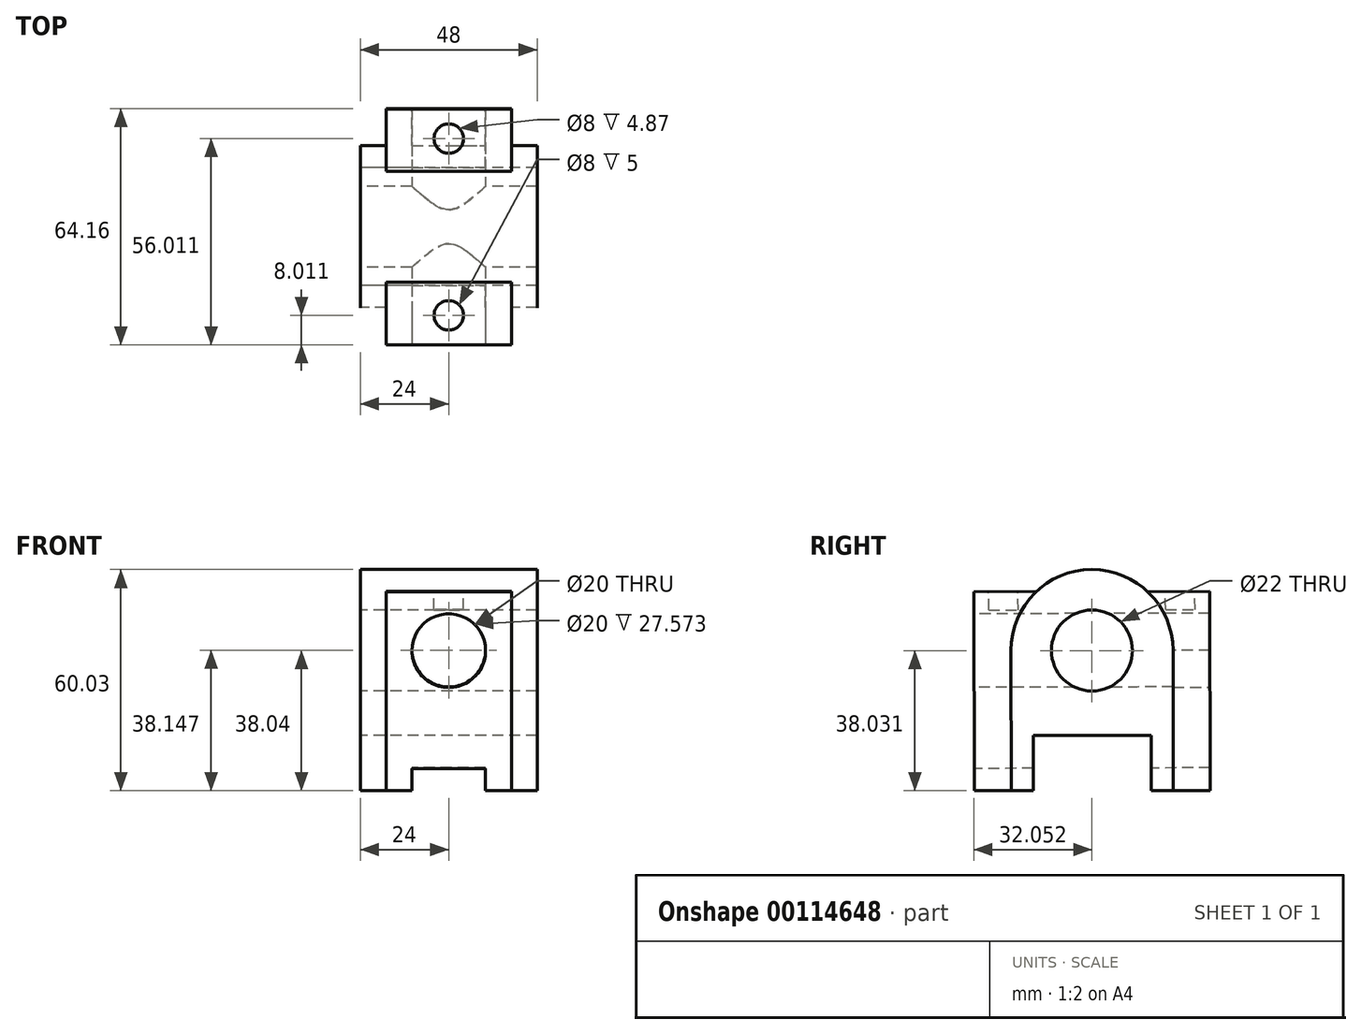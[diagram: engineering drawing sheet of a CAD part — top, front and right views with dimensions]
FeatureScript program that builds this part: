
annotation { "Feature Type Name" : "Feature", "Feature Type Description" : "" }
export const myFeature = defineFeature(function(context is Context, id is Id, definition is map)
    precondition{}
    {
        {
            var Q0;
            Q0=qCreatedBy(makeId("Right.planeOp"),FACE);
            var sketch = newSketch(context, id + "F0", { "sketchPlane" : qUnion([Q0])});
            skLineSegment(sketch, "E0.bottom", {"start": v(29.56, -52.26) * mm, "end": v(23.52, -52.26) * mm});
            skLineSegment(sketch, "E0.left", {"start": v(29.56, -52.26) * mm, "end": v(29.45, -14.14) * mm});
            skLineSegment(sketch, "E0.right", {"start": v(-14.44, -52.26) * mm, "end": v(-14.55, -14.25) * mm});
            skArc(sketch, "E1", {"start": v(29.45, -14.14) * mm, "mid": v(7.4, 7.74) * mm, "end": v(-14.55, -14.25) * mm});
            skLineSegment(sketch, "E2.top", {"start": v(23.52, -37.26) * mm, "end": v(-8.48, -37.26) * mm});
            skLineSegment(sketch, "E2.left", {"start": v(23.52, -52.26) * mm, "end": v(23.52, -37.26) * mm});
            skLineSegment(sketch, "E2.right", {"start": v(-8.48, -52.26) * mm, "end": v(-8.48, -37.26) * mm});
            skPoint(sketch, "E3", {"position": v(7.56, -52.26) * mm});
            skPoint(sketch, "E4", {"position": v(7.52, -37.26) * mm});
            skLineSegment(sketch, "E5.trimOffspring", {"start": v(-8.48, -52.26) * mm, "end": v(-14.44, -52.26) * mm});
            skCircle(sketch, "E6", {"center": v(7.45, -14.26) * mm, "radius": 11 * mm});
            skSolve(sketch);
        }
        {
            var Q0;
            Q0 = qSketchRegion(id + "F0", true);
            extrude(context, id + "F1", {"entities" : qUnion([Q0]), "endBound" : BoundingType.SYMMETRIC, "depth" : 48 * mm});
        }
        {
            var Q0;
            Q0=makeQuery(id+"F1.opExtrude","SWEPT_FACE",FACE,{"disambiguationData":[OSD([sQuery(id+"F0.wireOp",EDGE,"E0.right")])]});
            cPlane(context, id + "F2", {"entities" : qUnion([Q0]), "cplaneType" : CPlaneType.OFFSET, "offset" : 10 * mm, "width" : 150 * mm, "height" : 150 * mm});
        }
        {
            var Q0;
            Q0=qCreatedBy(id+"F2.planeOp",FACE);
            var sketch = newSketch(context, id + "F3", { "sketchPlane" : qUnion([Q0])});
            skLineSegment(sketch, "E7.top", {"start": v(-10, -46.22) * mm, "end": v(10, -46.22) * mm});
            skLineSegment(sketch, "E7.left", {"start": v(-10, -52.22) * mm, "end": v(-10, -46.22) * mm});
            skLineSegment(sketch, "E7.right", {"start": v(10, -52.22) * mm, "end": v(10, -46.22) * mm});
            skLineSegment(sketch, "E8", {"start": v(-17, -52.22) * mm, "end": v(-17, 1.78) * mm});
            skLineSegment(sketch, "E9", {"start": v(-17, 1.78) * mm, "end": v(17, 1.78) * mm});
            skLineSegment(sketch, "E10", {"start": v(17, 1.78) * mm, "end": v(17, -52.22) * mm});
            skLineSegment(sketch, "E11", {"start": v(17, -52.22) * mm, "end": v(10, -52.22) * mm});
            skPoint(sketch, "E12", {"position": v(0, -52.22) * mm});
            skCircle(sketch, "E13", {"center": v(0, -14.22) * mm, "radius": 10 * mm});
            skLineSegment(sketch, "E14.trimOffspring", {"start": v(-10, -52.22) * mm, "end": v(-17, -52.22) * mm});
            skSolve(sketch);
        }
        {
            var Q0;
            Q0=makeQuery(id+"F3.imprint","IMPRINT",FACE,{"disambiguationData":[TD([[makeQuery(id+"F3.imprint","IMPRINT",EDGE,{"derivedFrom":sQuery(id+"F3.wireOp",EDGE,"E7.top")}),1.0]])]});
            extrude(context, id + "F4", {"entities" : qUnion([Q0]), "operationType" : NewBodyOperationType.ADD, "endBound" : BoundingType.UP_TO_NEXT, "oppositeDirection" : true, "depth" : 25 * mm});
        }
        {
            var Q0;
            Q0=makeQuery(id+"F1.opExtrude","SWEPT_FACE",FACE,{"disambiguationData":[OSD([sQuery(id+"F0.wireOp",EDGE,"E0.left")])]});
            cPlane(context, id + "F5", {"entities" : qUnion([Q0]), "cplaneType" : CPlaneType.OFFSET, "offset" : 10 * mm, "width" : 150 * mm, "height" : 150 * mm});
        }
        {
            var Q0;
            Q0=qCreatedBy(id+"F5.planeOp",FACE);
            var sketch = newSketch(context, id + "F6", { "sketchPlane" : qUnion([Q0])});
            skLineSegment(sketch, "E15.bottom", {"start": v(-17, -52.35) * mm, "end": v(-10, -52.35) * mm});
            skLineSegment(sketch, "E15.top", {"start": v(-17, 1.65) * mm, "end": v(17, 1.65) * mm});
            skLineSegment(sketch, "E15.left", {"start": v(-17, -52.35) * mm, "end": v(-17, 1.65) * mm});
            skLineSegment(sketch, "E15.right", {"start": v(17, -52.35) * mm, "end": v(17, 1.65) * mm});
            skLineSegment(sketch, "E16.top", {"start": v(-10, -46.35) * mm, "end": v(10, -46.35) * mm});
            skLineSegment(sketch, "E16.left", {"start": v(-10, -52.35) * mm, "end": v(-10, -46.35) * mm});
            skLineSegment(sketch, "E16.right", {"start": v(10, -52.35) * mm, "end": v(10, -46.35) * mm});
            skPoint(sketch, "E17", {"position": v(0, -46.35) * mm});
            skCircle(sketch, "E18", {"center": v(0, -14.35) * mm, "radius": 10 * mm});
            skLineSegment(sketch, "E19.trimOffspring", {"start": v(10, -52.35) * mm, "end": v(17, -52.35) * mm});
            skSolve(sketch);
        }
        {
            var Q0;
            Q0 = qSketchRegion(id + "F6", true);
            extrude(context, id + "F7", {"entities" : qUnion([Q0]), "operationType" : NewBodyOperationType.ADD, "endBound" : BoundingType.UP_TO_NEXT, "oppositeDirection" : true, "depth" : 25 * mm});
        }
        {
            var Q0;
            Q0=makeQuery(id+"F4.opExtrude","SWEPT_FACE",FACE,{"disambiguationData":[OSD([sQuery(id+"F3.wireOp",EDGE,"E9")])]});
            var sketch = newSketch(context, id + "F8", { "sketchPlane" : qUnion([Q0])});
            skCircle(sketch, "E20", {"center": v(0, -16.6) * mm, "radius": 4 * mm});
            skCircle(sketch, "E21", {"center": v(0, 31.4) * mm, "radius": 4 * mm});
            skSolve(sketch);
        }
        {
            var Q0;
            Q0 = qSketchRegion(id + "F8", true);
            extrude(context, id + "F9", {"entities" : qUnion([Q0]), "operationType" : NewBodyOperationType.REMOVE, "oppositeDirection" : true, "depth" : 5 * mm});
        }
        {
            var Q0;
            Q0=makeQuery(id+"F4.opExtrude","CAP_FACE",FACE,{"disambiguationData":[OSD([sQuery(id+"F3.wireOp",EDGE,"E7.top"),sQuery(id+"F3.wireOp",EDGE,"E7.left"),sQuery(id+"F3.wireOp",EDGE,"E7.right"),sQuery(id+"F3.wireOp",EDGE,"E8"),sQuery(id+"F3.wireOp",EDGE,"E9"),sQuery(id+"F3.wireOp",EDGE,"E10"),sQuery(id+"F3.wireOp",EDGE,"E11"),sQuery(id+"F3.wireOp",EDGE,"E13"),sQuery(id+"F3.wireOp",EDGE,"E14.trimOffspring")])],"isStart":true});
            var sketch = newSketch(context, id + "F10", { "sketchPlane" : qUnion([Q0])});
            skCircle(sketch, "E22", {"center": v(0, -14.22) * mm, "radius": 10 * mm});
            skLineSegment(sketch, "E23.top", {"start": v(-10, -46.22) * mm, "end": v(10, -46.22) * mm});
            skLineSegment(sketch, "E23.left", {"start": v(-10, -52.22) * mm, "end": v(-10, -46.22) * mm});
            skLineSegment(sketch, "E23.right", {"start": v(10, -52.22) * mm, "end": v(10, -46.22) * mm});
            skLineSegment(sketch, "E24.top", {"start": v(10, -63.31) * mm, "end": v(-10, -63.31) * mm});
            skLineSegment(sketch, "E24.left", {"start": v(10, -52.22) * mm, "end": v(10, -63.31) * mm});
            skLineSegment(sketch, "E24.right", {"start": v(-10, -52.22) * mm, "end": v(-10, -63.31) * mm});
            skSolve(sketch);
        }
        {
            var Q0;
            Q0 = qSketchRegion(id + "F10", true);
            extrude(context, id + "F11", {"entities" : qUnion([Q0]), "operationType" : NewBodyOperationType.REMOVE, "endBound" : BoundingType.THROUGH_ALL, "oppositeDirection" : true, "depth" : 25 * mm});
        }
    });
